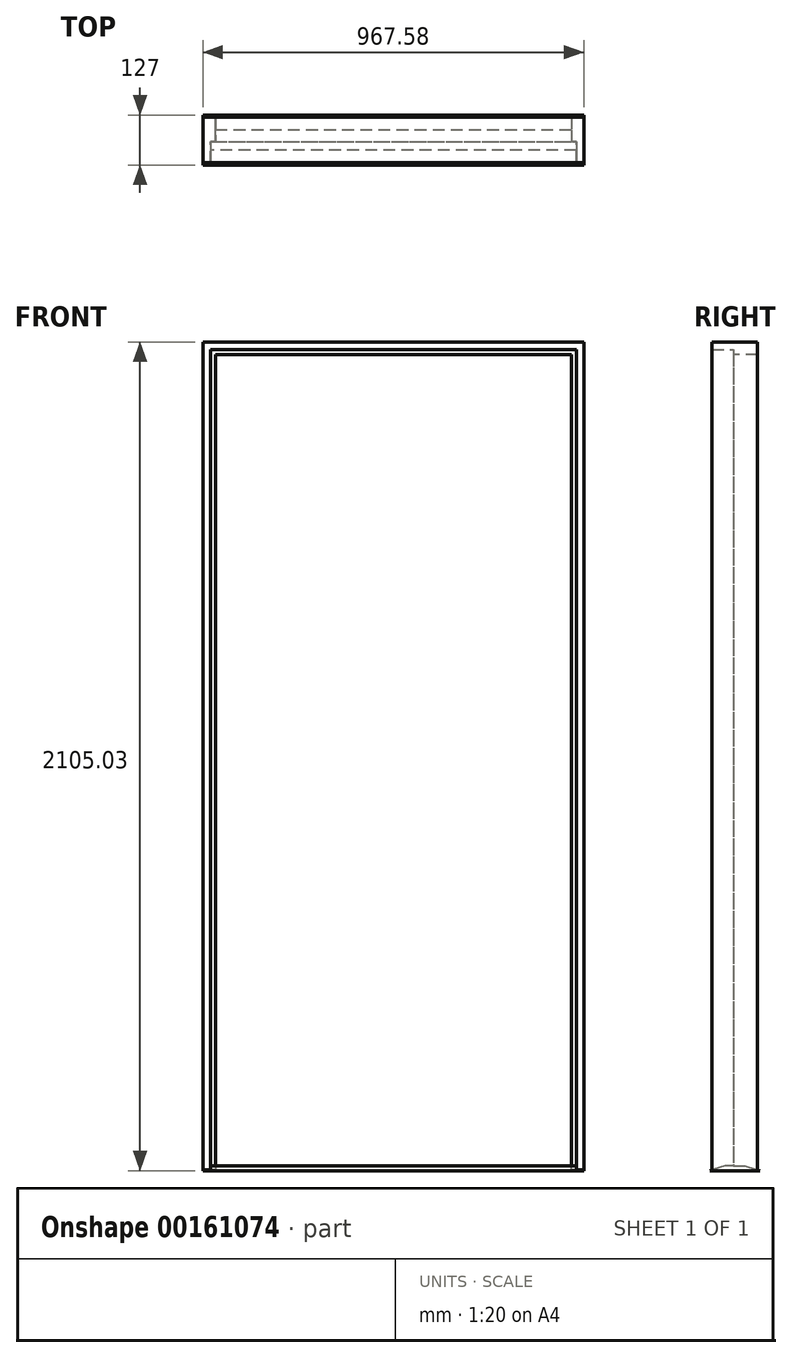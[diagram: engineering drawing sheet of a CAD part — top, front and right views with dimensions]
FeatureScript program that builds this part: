
annotation { "Feature Type Name" : "Feature", "Feature Type Description" : "" }
export const myFeature = defineFeature(function(context is Context, id is Id, definition is map)
    precondition{}
    {
        {
            var Q0;
            Q0=qCreatedBy(makeId("Front.planeOp"),FACE);
            cPlane(context, id + "F0", {"entities" : qUnion([Q0]), "cplaneType" : CPlaneType.OFFSET, "offset" : 3.17 * mm, "oppositeDirection" : true, "width" : 152.4 * mm, "height" : 152.4 * mm});
        }
        {
            var Q0;
            Q0=qCreatedBy(makeId("Front.planeOp"),FACE);
            var sketch = newSketch(context, id + "F1", { "sketchPlane" : qUnion([Q0])});
            skLineSegment(sketch, "E0.bottom", {"start": v(0, 0) * mm, "end": v(19.05, 0) * mm});
            skLineSegment(sketch, "E0.top", {"start": v(0, 2085.98) * mm, "end": v(19.05, 2085.98) * mm});
            skLineSegment(sketch, "E0.left", {"start": v(0, 0) * mm, "end": v(0, 2085.98) * mm});
            skLineSegment(sketch, "E0.right", {"start": v(19.05, 0) * mm, "end": v(19.05, 2085.98) * mm});
            skLineSegment(sketch, "E1.bottom", {"start": v(31.75, 2073.28) * mm, "end": v(19.05, 2073.28) * mm});
            skLineSegment(sketch, "E1.top", {"start": v(31.75, 0) * mm, "end": v(19.05, 0) * mm});
            skLineSegment(sketch, "E1.left", {"start": v(31.75, 2073.28) * mm, "end": v(31.75, 0) * mm});
            skLineSegment(sketch, "E1.right", {"start": v(19.05, 2073.28) * mm, "end": v(19.05, 0) * mm});
            skPoint(sketch, "E2.oppositeSnap0", {"position": v(9.53, 0) * mm});
            skLineSegment(sketch, "E3.left", {"start": v(19.05, 2085.98) * mm, "end": v(19.05, 2073.28) * mm});
            skLineSegment(sketch, "E4.top", {"start": v(967.58, 0) * mm, "end": v(948.53, 0) * mm});
            skLineSegment(sketch, "E4.left", {"start": v(967.58, 2105.03) * mm, "end": v(967.58, 0) * mm});
            skLineSegment(sketch, "E4.right", {"start": v(948.53, 2085.98) * mm, "end": v(948.53, 0) * mm});
            skLineSegment(sketch, "E5.bottom", {"start": v(948.53, 0) * mm, "end": v(935.83, 0) * mm});
            skLineSegment(sketch, "E5.top", {"start": v(948.53, 2073.28) * mm, "end": v(935.83, 2073.28) * mm});
            skLineSegment(sketch, "E5.left", {"start": v(948.53, 0) * mm, "end": v(948.53, 2073.28) * mm});
            skLineSegment(sketch, "E5.right", {"start": v(935.83, 0) * mm, "end": v(935.83, 2073.28) * mm});
            skLineSegment(sketch, "E6.bottom", {"start": v(19.05, 2085.98) * mm, "end": v(948.53, 2085.98) * mm});
            skLineSegment(sketch, "E6.top", {"start": v(19.05, 2073.28) * mm, "end": v(948.53, 2073.28) * mm});
            skLineSegment(sketch, "E6.right", {"start": v(948.53, 2085.98) * mm, "end": v(948.53, 2073.28) * mm});
            skLineSegment(sketch, "E7", {"start": v(0, 2085.98) * mm, "end": v(0, 2105.03) * mm});
            skLineSegment(sketch, "E8", {"start": v(0, 2105.03) * mm, "end": v(967.58, 2105.03) * mm});
            skLineSegment(sketch, "E9", {"start": v(948.53, 2085.98) * mm, "end": v(967.58, 2085.98) * mm});
            skSolve(sketch);
        }
        {
            var Q0;
            Q0=qCreatedBy(id+"F0.planeOp",FACE);
            var sketch = newSketch(context, id + "F2", { "sketchPlane" : qUnion([Q0])});
            skLineSegment(sketch, "E10.0", {"start": v(0, 0) * mm, "end": v(0, 2085.98) * mm});
            skLineSegment(sketch, "E11.0", {"start": v(0, 0) * mm, "end": v(19.05, 0) * mm});
            skLineSegment(sketch, "E12.0", {"start": v(31.75, 0) * mm, "end": v(19.05, 0) * mm});
            skLineSegment(sketch, "E13.0", {"start": v(31.75, 2073.28) * mm, "end": v(31.75, 0) * mm});
            skLineSegment(sketch, "E14.0", {"start": v(19.05, 2073.28) * mm, "end": v(948.53, 2073.28) * mm});
            skLineSegment(sketch, "E15.0", {"start": v(935.83, 0) * mm, "end": v(935.83, 2073.28) * mm});
            skLineSegment(sketch, "E16.0", {"start": v(948.53, 0) * mm, "end": v(935.83, 0) * mm});
            skLineSegment(sketch, "E17.0", {"start": v(967.58, 0) * mm, "end": v(948.53, 0) * mm});
            skLineSegment(sketch, "E18.0", {"start": v(0, 2085.98) * mm, "end": v(0, 2105.03) * mm});
            skLineSegment(sketch, "E19.0", {"start": v(0, 2105.03) * mm, "end": v(967.58, 2105.03) * mm});
            skLineSegment(sketch, "E20.0", {"start": v(967.58, 2105.03) * mm, "end": v(967.58, 0) * mm});
            skSolve(sketch);
        }
        {
            var Q0;
            Q0=qSketchRegion(id+"F2",true);
            extrude(context, id + "F3", {"entities" : qUnion([Q0]), "oppositeDirection" : true, "depth" : 61.9 * mm});
        }
        {
            var Q0;
            Q0=qCreatedBy(makeId("Front.planeOp"),FACE);
            var sketch = newSketch(context, id + "F4", { "sketchPlane" : qUnion([Q0])});
            skLineSegment(sketch, "E21.0", {"start": v(0, 0) * mm, "end": v(19.05, 0) * mm});
            skLineSegment(sketch, "E22.0", {"start": v(19.05, 2073.28) * mm, "end": v(19.05, 0) * mm});
            skLineSegment(sketch, "E23.0", {"start": v(0, 0) * mm, "end": v(0, 2085.98) * mm});
            skLineSegment(sketch, "E24.0", {"start": v(19.05, 2085.98) * mm, "end": v(19.05, 2073.28) * mm});
            skLineSegment(sketch, "E25.0", {"start": v(19.05, 2085.98) * mm, "end": v(948.53, 2085.98) * mm});
            skLineSegment(sketch, "E26.0", {"start": v(948.53, 2085.98) * mm, "end": v(948.53, 0) * mm});
            skLineSegment(sketch, "E27.0", {"start": v(967.58, 0) * mm, "end": v(948.53, 0) * mm});
            skPoint(sketch, "E28.0", {"position": v(0, 2095.5) * mm});
            skLineSegment(sketch, "E29.0", {"start": v(0, 2085.98) * mm, "end": v(0, 2105.03) * mm});
            skLineSegment(sketch, "E30.0", {"start": v(0, 2105.03) * mm, "end": v(967.58, 2105.03) * mm});
            skLineSegment(sketch, "E31.0", {"start": v(967.58, 2105.03) * mm, "end": v(967.58, 0) * mm});
            skSolve(sketch);
        }
        {
            var Q0;
            Q0=qSketchRegion(id+"F4",true);
            extrude(context, id + "F5", {"entities" : qUnion([Q0]), "operationType" : NewBodyOperationType.ADD, "depth" : 50.8 * mm, "hasSecondDirection" : true, "secondDirectionOppositeDirection" : true, "secondDirectionDepth" : 3.17 * mm});
        }
        {
            var Q0;
            Q0=qCreatedBy(makeId("Right.planeOp"),FACE);
            var sketch = newSketch(context, id + "F6", { "sketchPlane" : qUnion([Q0])});
            skLineSegment(sketch, "E32", {"start": v(-18.26, 12.7) * mm, "end": v(32.54, 12.7) * mm});
            skLineSegment(sketch, "E33", {"start": v(-56.36, 0) * mm, "end": v(-18.26, 12.7) * mm});
            skLineSegment(sketch, "E34", {"start": v(32.54, 12.7) * mm, "end": v(70.64, 0) * mm});
            skLineSegment(sketch, "E35.0", {"start": v(65.09, 0) * mm, "end": v(-50.8, 0) * mm});
            skLineSegment(sketch, "E36", {"start": v(7.14, 0) * mm, "end": v(70.64, 0) * mm});
            skLineSegment(sketch, "E37", {"start": v(7.14, 0) * mm, "end": v(-56.36, 0) * mm});
            skSolve(sketch);
        }
        {
            var Q0;
            Q0=qSketchRegion(id+"F6",true);
            var Q1;
            Q1=makeQuery(id+"F5.boolean.opBoolean","MERGE",FACE,{"derivedFrom":[makeQuery(id+"F3.opExtrude","SWEPT_FACE",FACE,{"disambiguationData":[OSD([sQuery(id+"F2.wireOp",EDGE,"E20.0")])]}),makeQuery(id+"F5.opExtrude","SWEPT_FACE",FACE,{"disambiguationData":[OSD([sQuery(id+"F4.wireOp",EDGE,"E31.0")])]})]});
            extrude(context, id + "F7", {"entities" : qUnion([Q0]), "operationType" : NewBodyOperationType.ADD, "endBound" : BoundingType.UP_TO_SURFACE, "endBoundEntityFace" : qUnion([Q1]), "depth" : 25.4 * mm});
        }
    });
